# Revit family: 712-0065-04-201-DN150
name_source: partatom
category: Pipe Fittings
units: mm (PartAtom-declared; Revit-internal decimal feet)

## family parameters
Always vertical = Yes
Cut with Voids When Loaded = No
Part Type = Elbow
Round Connector Dimension = Use Diameter
Shared = No
Work Plane-Based = No

## types (1)
- DN150_PN10/16
    Body_wallthickness = 165 mm  [stored 0.541339 ft]
    DN 150_PN10/16 = 712-0150-04-201
    DN150_PN10/16 = Yes
    Description_ = AVK FLANGED PIPE W/LOOSE FLANGES
    FOD = 143 mm
    Flange_thickness = 20 mm  [stored 0.0656168 ft]
    ID(Radius) = 75 mm
    L = 160 mm  [stored 0.524934 ft]
    L_Ref = 100 mm  [stored 0.328084 ft]
    Nominal Diameter(DN) = 150 mm  [stored 0.492126 ft]
    RF_Thick = 4 mm  [stored 0.0131234 ft]
    Rf_Dia = 106 mm
    Search_Table = 712-0420-001-DN40-300
    URL product pages = https://www.avkvalves.com

note: [stored X ft] marks values corroborated as IEEE doubles in the binary element streams (Revit-internal decimal feet)

## geometry (parser evidence)
native form markers: Sweep x8
no freeform markers — native parametric forms only
